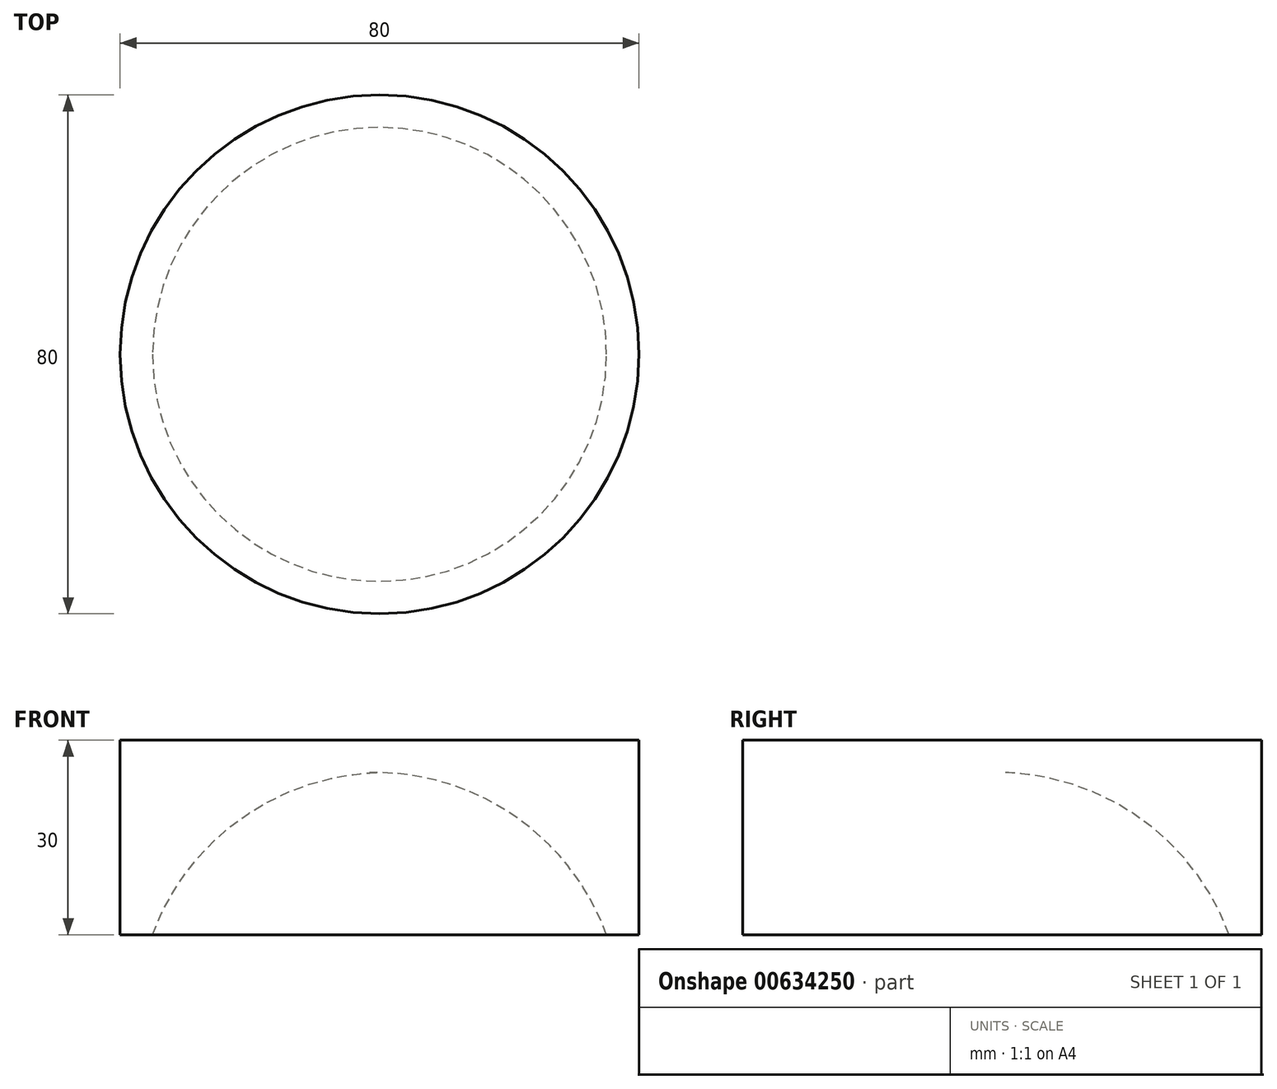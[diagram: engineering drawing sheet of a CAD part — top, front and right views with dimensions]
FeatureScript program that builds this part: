
annotation { "Feature Type Name" : "Feature", "Feature Type Description" : "" }
export const myFeature = defineFeature(function(context is Context, id is Id, definition is map)
    precondition{}
    {
        {
            var Q0;
            Q0=qCreatedBy(makeId("Front.planeOp"),FACE);
            var sketch = newSketch(context, id + "F0", { "sketchPlane" : qUnion([Q0])});
            skArc(sketch, "E0", {"start": v(0, 25) * mm, "mid": v(-21.37, 17.91) * mm, "end": v(-35, 0) * mm});
            skLineSegment(sketch, "E1", {"start": v(0, 25) * mm, "end": v(0, 30) * mm});
            skLineSegment(sketch, "E2", {"start": v(-35, 0) * mm, "end": v(-40, 0) * mm});
            skLineSegment(sketch, "E3", {"start": v(-40, 0) * mm, "end": v(-40, 30) * mm});
            skLineSegment(sketch, "E4", {"start": v(0, 30) * mm, "end": v(-40, 30) * mm});
            skSolve(sketch);
        }
        {
            var Q0;
            Q0=makeQuery(id+"F0.imprint","IMPRINT",FACE,{"disambiguationData":[TD([[makeQuery(id+"F0.imprint","IMPRINT",EDGE,{"derivedFrom":sQuery(id+"F0.wireOp",EDGE,"E0")}),-1.0]])]});
            var Q1;
            Q1=sQuery(id+"F0.wireOp",EDGE,"E1");
            revolve(context, id + "F1", {"entities" : qUnion([Q0]), "axis" : qUnion([Q1]), "revolveType" : RevolveType.FULL});
        }
    });
